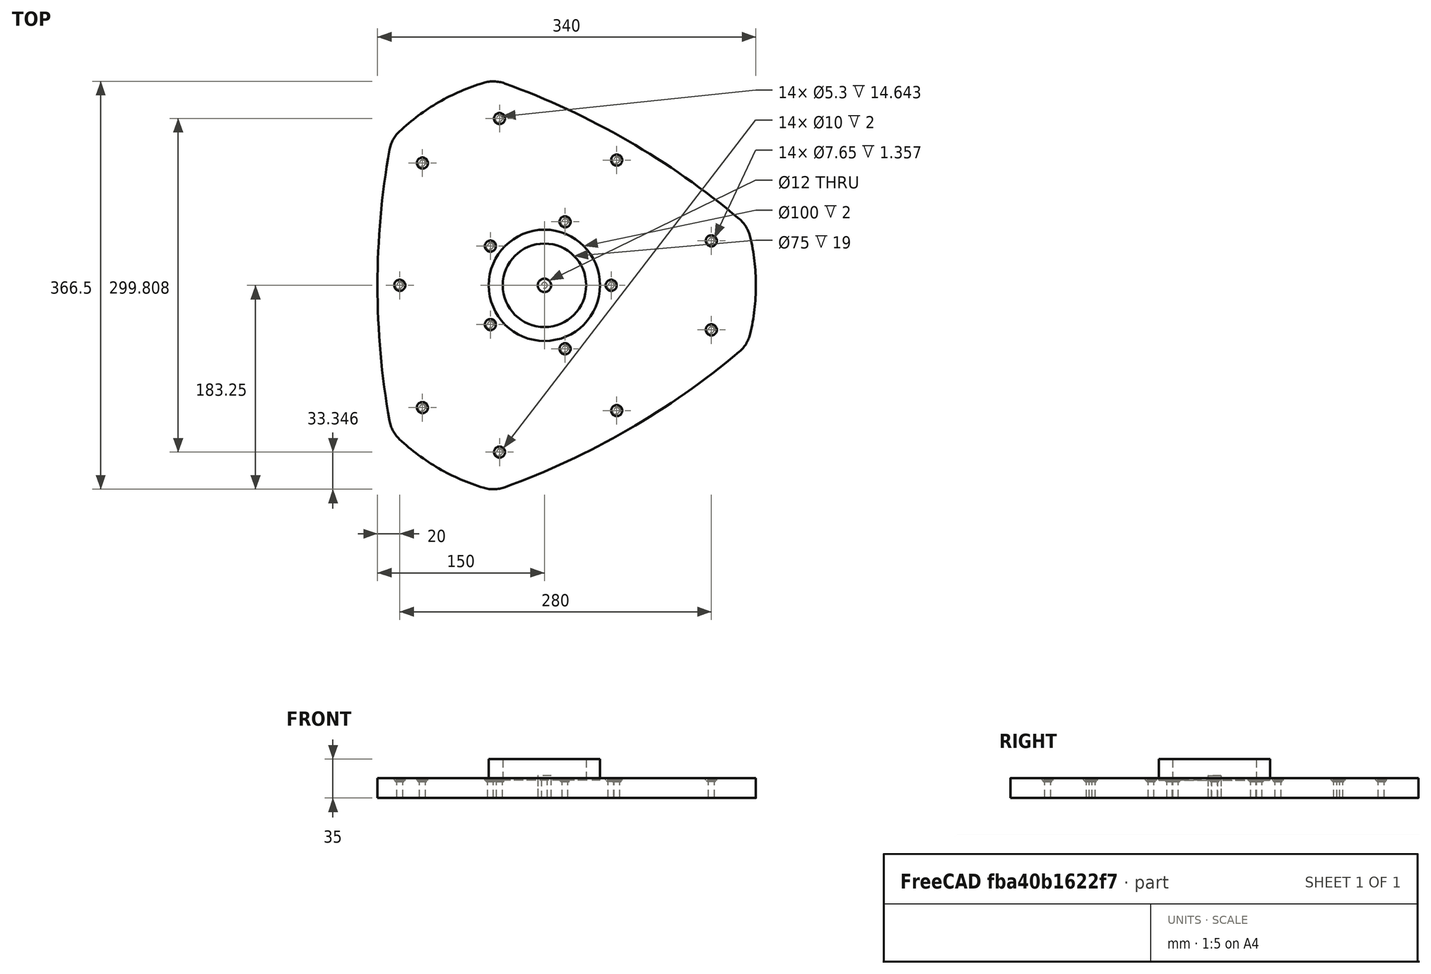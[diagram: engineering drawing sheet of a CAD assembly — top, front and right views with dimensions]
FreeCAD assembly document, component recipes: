
FREECAD ASSEMBLY — COMPONENT RECIPES ("composit_stand3_basement_amplifier_model")

This assembly document has 3 components, labeled P0..P2 below (a component is one placed body or linked part). 2 of them carry a construction recipe — the FreeCAD feature program that regenerates the part from scratch, quoted from this document or its linked companion documents; the rest are supplied as boundary geometry only. No exploded tour is included for this assembly.
COMPONENT P0 — geometry summary ("axis_bolt"; no construction recipe available for this part):
  bounding box: 20.0 x 12.0 x 12.0 mm
  tessellated surface: 500 triangles
  volume: 2262 mm^3 (79% of its bounding box)
  symmetry: 2-fold rotationally symmetric about the y axis; revolution-symmetric about the z axis through its bounding-box center; mirror-symmetric across its z mid-plane
COMPONENT P1 — recipe-attached ("Body", modeled in this document).
Construction recipe (the document's own serialized feature program — sketch geometry with constraints, then the solid features built on it; lengths are millimeters unless a unit is written):

FEATURE [PartDesign::SubShapeBinder] Binder001
  BindCopyOnChange = 0
  BindMode = 0
  ClaimChildren = true
  Context = -> Body [Binder001.]
  Fuse = false
  MakeFace = false
  OffsetFill = false
  OffsetIntersection = false
  OffsetJoinType = 0
  OffsetOpenResult = false
  PartialLoad = false
  Relative = true
  Support = -> [Connect]
  _Version = 2
FEATURE [PartDesign::Pad] Pad
  Direction = (0,0,1)
  Length = 18
  Length2 = 10
  Profile = -> Binder001
  Refine = true
  Suppressed = false
  Type = 0
FEATURE [PartDesign::CoordinateSystem] Local_CS  label="bottom_LCS"
  AttacherType = Attacher::AttachEngine3D
  AttachmentSupport = -> [XY_Plane]
  MapMode = 5
FEATURE [PartDesign::CoordinateSystem] Local_CS001  label="top_LCS"
  AttacherType = Attacher::AttachEngine3D
  AttachmentOffset = pos=(0,0,18) rot=(0,0,1;0rad)
  AttachmentSupport = -> [XY_Plane]
  MapMode = 5
  Placement = pos=(0,0,18) rot=(0,0,1;0rad)
FEATURE [PartDesign::CoordinateSystem] Local_CS002  label="bearing_LCS"
  AttacherType = Attacher::AttachEngine3D
  AttachmentOffset = pos=(0,0,16) rot=(0,0,1;0rad)
  AttachmentSupport = -> [XY_Plane]
  MapMode = 5
  Placement = pos=(0,0,16) rot=(0,0,1;0rad)
  expr: AttachmentOffset = <<bearing_placement>>.LinkedObject.Placement
FEATURE [PartDesign::Boolean] Boolean
  BaseFeature = -> Pad
  Group = -> [Fusion]
  Suppressed = false
  Type = 1
  UsePlacement = true
FEATURE [PartDesign::Body] Body  label="amplifier"
  AllowCompound = false
  Group = -> [Binder001,Pad,Boolean,Local_CS,Local_CS001,Local_CS002]
  Origin = -> Origin
  Tip = -> Boolean
COMPONENT P2 — same part as P1; its construction recipe is shown at P1.
PROVENANCE & LICENSES
A FreeCAD (.FCStd) document from a public repository crawl; recipes are the document's own serialized feature recipes (and, for linked parts, companion documents' recipes).
License: as declared in the source repository (recorded in the dataset sidecar).
